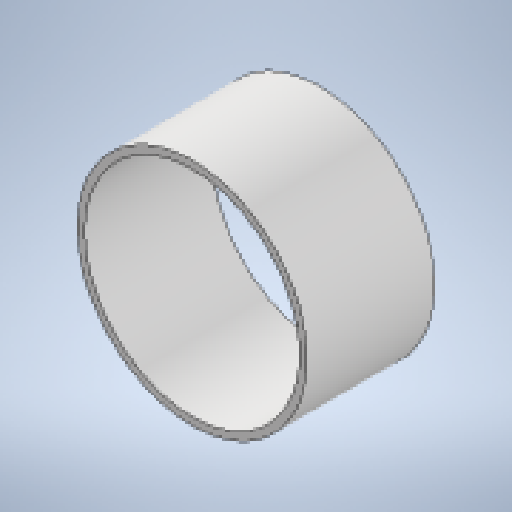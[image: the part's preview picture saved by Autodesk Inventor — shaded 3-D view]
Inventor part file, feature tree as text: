
AUTODESK INVENTOR PART (.ipt)
format: ipt  version: 2025.1 (Build 291241020, 241B)  size: 146,944 bytes
history: native  units: mm
features: extrude x1, sketch x1
ambient origin geometry x8: Origin, YZ Plane, XZ Plane, XY Plane, X Axis, Y Axis, Z Axis, Center Point
bodies: Solid1 (feature_tree)
feature tree (2):
  extrude  "Extrusion1"  Depth=50.0mm
  sketch  "Sketch1"  dims[d0=90.0mm d1=3.0mm d2=50.0mm d3=0.0mm]
